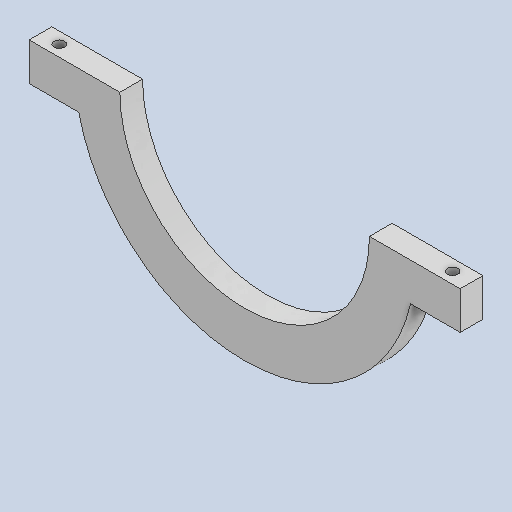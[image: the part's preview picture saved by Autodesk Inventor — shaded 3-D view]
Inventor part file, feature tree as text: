
AUTODESK INVENTOR PART (.ipt)
format: ipt  version: 2025 (Build 290162010, 162A)  size: 158,208 bytes
history: native  units: mm
features: extrude x2, sketch x2, mirror x1, other x1
ambient origin geometry x8: Origin, YZ Plane, XZ Plane, XY Plane, X Axis, Y Axis, Z Axis, Center Point
bodies: Solid1 (feature_tree)
feature tree (6):
  extrude  "Extrusion1"  Depth=30.0mm
  extrude  "Extrusion7"  Depth=50.0mm
  mirror  "Mirror1"
  sketch  "Sketch1"  dims[d2=30.0mm d3=0.0mm d13=390.0mm]
  sketch  "Sketch7"  dims[d26=80.0mm d36=60.0mm d40=60.0mm d41=50.0mm d42=14.0mm d43=25.0mm d44=0.0mm d45=0.0mm]
  other  "Definition1"
